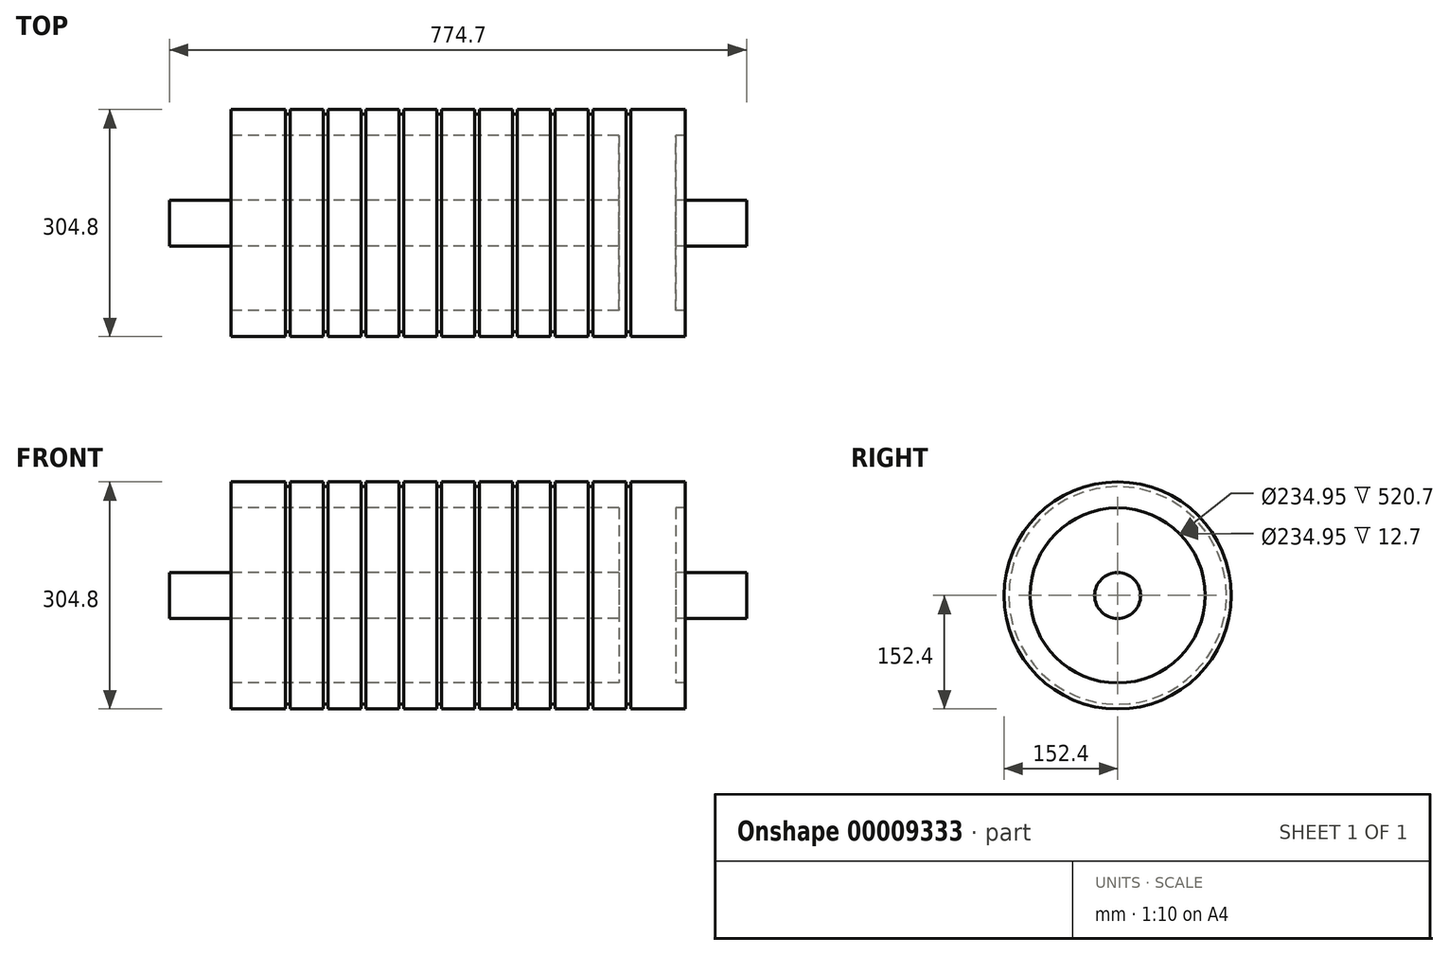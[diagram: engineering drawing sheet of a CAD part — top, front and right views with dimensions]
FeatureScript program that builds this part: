
annotation { "Feature Type Name" : "Feature", "Feature Type Description" : "" }
export const myFeature = defineFeature(function(context is Context, id is Id, definition is map)
    precondition{}
    {
        {
            var Q0;
            Q0=qCreatedBy(makeId("Front.planeOp"),FACE);
            var sketch = newSketch(context, id + "F0", { "sketchPlane" : qUnion([Q0])});
            skLineSegment(sketch, "E0", {"start": v(-304.8, 0) * mm, "end": v(304.8, 0) * mm, "construction": true});
            skLineSegment(sketch, "E1.0", {"start": v(-304.8, 117.48) * mm, "end": v(304.8, 117.48) * mm});
            skLineSegment(sketch, "E2.0", {"start": v(-304.8, 152.4) * mm, "end": v(-231.78, 152.4) * mm});
            skLineSegment(sketch, "E3", {"start": v(-304.8, 152.4) * mm, "end": v(-304.8, 117.48) * mm});
            skLineSegment(sketch, "E4", {"start": v(304.8, 152.4) * mm, "end": v(304.8, 117.48) * mm});
            skLineSegment(sketch, "E5.0", {"start": v(-231.78, 152.4) * mm, "end": v(-231.78, 146.05) * mm});
            skLineSegment(sketch, "E6.0", {"start": v(-225.43, 152.4) * mm, "end": v(-225.43, 146.05) * mm});
            skLineSegment(sketch, "E7.0", {"start": v(-231.78, 146.05) * mm, "end": v(-225.43, 146.05) * mm});
            skLineSegment(sketch, "E8.trimOffspring", {"start": v(-225.43, 152.4) * mm, "end": v(-180.97, 152.4) * mm});
            skLineSegment(sketch, "E9.1.0.0", {"start": v(-180.97, 152.4) * mm, "end": v(-180.97, 146.05) * mm});
            skLineSegment(sketch, "E9.1.0.1", {"start": v(-174.62, 152.4) * mm, "end": v(-174.62, 146.05) * mm});
            skLineSegment(sketch, "E9.1.0.2", {"start": v(-180.97, 146.05) * mm, "end": v(-174.62, 146.05) * mm});
            skLineSegment(sketch, "E9.2.0.0", {"start": v(-130.17, 152.4) * mm, "end": v(-130.17, 146.05) * mm});
            skLineSegment(sketch, "E9.2.0.1", {"start": v(-123.82, 152.4) * mm, "end": v(-123.82, 146.05) * mm});
            skLineSegment(sketch, "E9.2.0.2", {"start": v(-130.17, 146.05) * mm, "end": v(-123.82, 146.05) * mm});
            skLineSegment(sketch, "E9.3.0.0", {"start": v(-79.37, 152.4) * mm, "end": v(-79.37, 146.05) * mm});
            skLineSegment(sketch, "E9.3.0.1", {"start": v(-73.02, 152.4) * mm, "end": v(-73.02, 146.05) * mm});
            skLineSegment(sketch, "E9.3.0.2", {"start": v(-79.37, 146.05) * mm, "end": v(-73.02, 146.05) * mm});
            skLineSegment(sketch, "E9.4.0.0", {"start": v(-28.57, 152.4) * mm, "end": v(-28.57, 146.05) * mm});
            skLineSegment(sketch, "E9.4.0.1", {"start": v(-22.22, 152.4) * mm, "end": v(-22.22, 146.05) * mm});
            skLineSegment(sketch, "E9.4.0.2", {"start": v(-28.57, 146.05) * mm, "end": v(-22.22, 146.05) * mm});
            skLineSegment(sketch, "E9.5.0.0", {"start": v(22.23, 152.4) * mm, "end": v(22.23, 146.05) * mm});
            skLineSegment(sketch, "E9.5.0.1", {"start": v(28.58, 152.4) * mm, "end": v(28.58, 146.05) * mm});
            skLineSegment(sketch, "E9.5.0.2", {"start": v(22.23, 146.05) * mm, "end": v(28.58, 146.05) * mm});
            skLineSegment(sketch, "E9.6.0.0", {"start": v(73.03, 152.4) * mm, "end": v(73.03, 146.05) * mm});
            skLineSegment(sketch, "E9.6.0.1", {"start": v(79.38, 152.4) * mm, "end": v(79.38, 146.05) * mm});
            skLineSegment(sketch, "E9.6.0.2", {"start": v(73.03, 146.05) * mm, "end": v(79.38, 146.05) * mm});
            skLineSegment(sketch, "E9.7.0.0", {"start": v(123.83, 152.4) * mm, "end": v(123.83, 146.05) * mm});
            skLineSegment(sketch, "E9.7.0.1", {"start": v(130.18, 152.4) * mm, "end": v(130.18, 146.05) * mm});
            skLineSegment(sketch, "E9.7.0.2", {"start": v(123.83, 146.05) * mm, "end": v(130.18, 146.05) * mm});
            skLineSegment(sketch, "E9.8.0.0", {"start": v(174.63, 152.4) * mm, "end": v(174.63, 146.05) * mm});
            skLineSegment(sketch, "E9.8.0.1", {"start": v(180.98, 152.4) * mm, "end": v(180.98, 146.05) * mm});
            skLineSegment(sketch, "E9.8.0.2", {"start": v(174.63, 146.05) * mm, "end": v(180.98, 146.05) * mm});
            skLineSegment(sketch, "E9.9.0.0", {"start": v(225.43, 152.4) * mm, "end": v(225.43, 146.05) * mm});
            skLineSegment(sketch, "E9.9.0.1", {"start": v(231.78, 152.4) * mm, "end": v(231.78, 146.05) * mm});
            skLineSegment(sketch, "E9.9.0.2", {"start": v(225.43, 146.05) * mm, "end": v(231.78, 146.05) * mm});
            skLineSegment(sketch, "E9.direction1", {"start": v(-231.78, 146.05) * mm, "end": v(-180.97, 146.05) * mm, "construction": true});
            skLineSegment(sketch, "E10.trimOffspring", {"start": v(-174.63, 152.4) * mm, "end": v(-130.17, 152.4) * mm});
            skLineSegment(sketch, "E11.trimOffspring", {"start": v(-123.83, 152.4) * mm, "end": v(-79.37, 152.4) * mm});
            skLineSegment(sketch, "E12.trimOffspring", {"start": v(-73.02, 152.4) * mm, "end": v(-28.57, 152.4) * mm});
            skLineSegment(sketch, "E13.trimOffspring", {"start": v(-22.22, 152.4) * mm, "end": v(22.23, 152.4) * mm});
            skLineSegment(sketch, "E14.trimOffspring", {"start": v(79.38, 152.4) * mm, "end": v(123.83, 152.4) * mm});
            skLineSegment(sketch, "E15.trimOffspring", {"start": v(28.58, 152.4) * mm, "end": v(73.03, 152.4) * mm});
            skLineSegment(sketch, "E16.trimOffspring", {"start": v(130.18, 152.4) * mm, "end": v(174.63, 152.4) * mm});
            skLineSegment(sketch, "E17.trimOffspring", {"start": v(180.98, 152.4) * mm, "end": v(225.43, 152.4) * mm});
            skLineSegment(sketch, "E18.trimOffspring", {"start": v(231.78, 152.4) * mm, "end": v(304.8, 152.4) * mm});
            skLineSegment(sketch, "E19.bottom", {"start": v(-292.1, 117.48) * mm, "end": v(-215.9, 117.48) * mm});
            skLineSegment(sketch, "E19.top", {"start": v(-292.1, 30.86) * mm, "end": v(-215.9, 30.86) * mm});
            skLineSegment(sketch, "E19.left", {"start": v(-292.1, 117.48) * mm, "end": v(-292.1, 30.86) * mm});
            skLineSegment(sketch, "E19.right", {"start": v(-215.9, 117.48) * mm, "end": v(-215.9, 30.86) * mm});
            skLineSegment(sketch, "E20", {"start": v(0, 0) * mm, "end": v(0, 259.5) * mm, "construction": true});
            skLineSegment(sketch, "E21.0", {"start": v(-387.35, 0) * mm, "end": v(-387.35, 259.5) * mm});
            skLineSegment(sketch, "E22.bottom", {"start": v(-387.35, 30.86) * mm, "end": v(0, 30.86) * mm});
            skLineSegment(sketch, "E22.top", {"start": v(-387.35, 0) * mm, "end": v(0, 0) * mm});
            skLineSegment(sketch, "E22.left", {"start": v(-387.35, 30.86) * mm, "end": v(-387.35, 0) * mm});
            skLineSegment(sketch, "E22.right", {"start": v(0, 30.86) * mm, "end": v(0, 0) * mm});
            skLineSegment(sketch, "E23.0.MirrorCS", {"start": v(215.9, 117.48) * mm, "end": v(215.9, 30.86) * mm});
            skLineSegment(sketch, "E24.0.MirrorCS", {"start": v(292.1, 117.48) * mm, "end": v(292.1, 30.86) * mm});
            skLineSegment(sketch, "E25.0.MirrorCS", {"start": v(387.35, 30.86) * mm, "end": v(0, 30.86) * mm});
            skLineSegment(sketch, "E26.0.MirrorCS", {"start": v(387.35, 0) * mm, "end": v(387.35, 259.5) * mm});
            skLineSegment(sketch, "E27.0.MirrorCS", {"start": v(387.35, 0) * mm, "end": v(0, 0) * mm});
            skSolve(sketch);
        }
        {
            var Q0;
            Q0=makeQuery(id+"F0.imprint","IMPRINT",FACE,{"disambiguationData":[TD([[makeQuery(id+"F0.imprint","IMPRINT",EDGE,{"derivedFrom":sQuery(id+"F0.wireOp",EDGE,"E2.0")}),-1.0]])]});
            var Q1;
            {var subQ2=sQuery(id+"F0.wireOp",EDGE,"E23.0.MirrorCS");Q1=makeQuery(id+"F0.imprint","IMPRINT",FACE,{"disambiguationData":[TD([[makeQuery(id+"F0.imprint","IMPRINT",EDGE,{"derivedFrom":subQ2}),1.0]])]});}
            var Q2;
            Q2=makeQuery(id+"F0.imprint","IMPRINT",FACE,{"disambiguationData":[TD([[makeQuery(id+"F0.imprint","IMPRINT",EDGE,{"derivedFrom":sQuery(id+"F0.wireOp",EDGE,"E19.bottom")}),-1.0]])]});
            var Q3;
            {var subQ1=sQuery(id+"F0.wireOp",EDGE,"E27.0.MirrorCS");Q3=makeQuery(id+"F0.imprint","IMPRINT",FACE,{"disambiguationData":[TD([[makeQuery(id+"F0.imprint","IMPRINT",EDGE,{"derivedFrom":subQ1}),-1.0]])]});}
            var Q4;
            Q4=makeQuery(id+"F0.imprint","IMPRINT",FACE,{"disambiguationData":[TD([[makeQuery(id+"F0.imprint","IMPRINT",EDGE,{"derivedFrom":sQuery(id+"F0.wireOp",EDGE,"E22.top")}),1.0]])]});
            var Q5;
            Q5=sQuery(id+"F0.wireOp",EDGE,"E22.top");
            revolve(context, id + "F1", {"entities" : qUnion([Q0, Q1, Q2, Q3, Q4]), "axis" : qUnion([Q5]), "revolveType" : RevolveType.FULL});
        }
    });
